MODEL slx_886a84f6ba0e
CONFIG AbsTol = auto
CONFIG EnableMultiTasking = off
CONFIG FixedStep = auto
CONFIG InitFcn = Wn = 10;
zeta = 0.4;
T = 0.001
CONFIG MaxStep = auto
CONFIG MinStep = auto
CONFIG RelTol = 1e-3
CONFIG SampleTimeConstraint = Unconstrained
CONFIG SolverName = VariableStepAuto
CONFIG StartTime = 0.0
CONFIG StopTime = 5
BLOCK [CCaller] C Caller1
  FunctionName = Damping_Loop
  PortSpecificationStruct = %)30     .    X ,   8    (     @         %    "     (    !     0         %  0 "0    $    _    07)G3F%M90  4&]R=$YA;64 4V-O<&4     26YD97@     5'EP90      4VEZ90      27-';&]B86P   X    X    !@    @    $          4    (     0    4    !         !     %    :6YP=70    .    .     8    (    !          %    "     $    %     0         0    !0   &EN<'5T    #@   #@    &    "     0         !0    @    !    !0...<+936ch>
BLOCK [Constant] Constant
BLOCK [DataTypeConversion] Data Type Conversion1
  RndMeth = Floor
  SaturateOnIntegerOverflow = off
BLOCK [DiscreteTransferFcn] Discrete Transfer Fcn6
  CloseFcn = dspblkCoreblockFVToolHelper(gcbh,'close');
  CopyFcn = dspblkCoreblockFVToolHelper(gcbh,'copy');
  DeleteFcn = dspblkCoreblockFVToolHelper(gcbh,'close');
  Denominator = [(T^2*Wn^2+4*T*Wn*zeta+4) (-8+2*T^2*Wn^2) (4+T^2*Wn^2-4*T*Wn*zeta)]
  InputPortMap = u0
  LoadFcn = dspblkCoreblockFVToolHelper(gcbh,'load');
  ModelCloseFcn = dspblkCoreblockFVToolHelper(gcbh,'close');
  Numerator = [(T^2*Wn^2) (2*T^2*Wn^2) T^2*Wn^2]
  PostSaveFcn = dspblkCoreblockFVToolHelper(gcbh,'postsave');
  PreSaveFcn = dspblkCoreblockFVToolHelper(gcbh,'presave');
BLOCK [Scope] Scope3
  ActiveDisplayYMaximum = 1.2254615103638327
  ActiveDisplayYMinimum = -0.24415285715070134
  DataLoggingVariableName = ScopeData3
  Floating = off
  GraphicalSettings = {"Style":{"BackgroundColor":[0.12941176470588237,0.12941176470588237,0.12941176470588237],"AxesColor":[0.07058823529411765,0.07058823529411765,0.07058823529411765],"LabelsColor":[0.8509803921568627,0.8509803921568627,0.8509803921568627],"PreserveColors":false,"Visible":[true,true,true],"LineStyle":["-","-","-"],"LineWidth":[1.5,1.5,1.5],"BarWidth":[0.9,0.9,0.9],"LineColor":["auto","auto","auto"],"...<+2272ch>
  MultipleDisplayCache = [{"MaxYLimMag":1.173661687403794,"MaxYLimReal":1.2254615103638327,"MinYLimMag":0,"MinYLimReal":-0.24415285715070134,"PlotAsMagnitudePhase":false,"ShowGrid":true,"ShowLegend":true,"Title":"%<SignalLabel>","YLabel":""}]
  NumInputPorts = 3
  ScopeFrameLocation = window
  ShowLegend = on
  WasSavedAsWebScope = on
  WindowPosition = [871.000000,337.000000,560.000000,420.000000,]
BLOCK [TransferFcn] Transfer Fcn9
  Denominator = [1 2*zeta*Wn Wn^2]
  Numerator = [Wn^2]
BLOCK [ZeroOrderHold] Zero-Order Hold4
  SampleTime = 0.001
LINE C Caller1:1 -> Scope3:3
LINE Constant:1 -> Transfer Fcn9:1
LINE Constant:1 -> Zero-Order Hold4:1
LINE Data Type Conversion1:1 -> C Caller1:1
LINE Discrete Transfer Fcn6:1 -> Scope3:2
LINE Transfer Fcn9:1 -> Scope3:1
LINE Zero-Order Hold4:1 -> Data Type Conversion1:1
LINE Zero-Order Hold4:1 -> Discrete Transfer Fcn6:1
